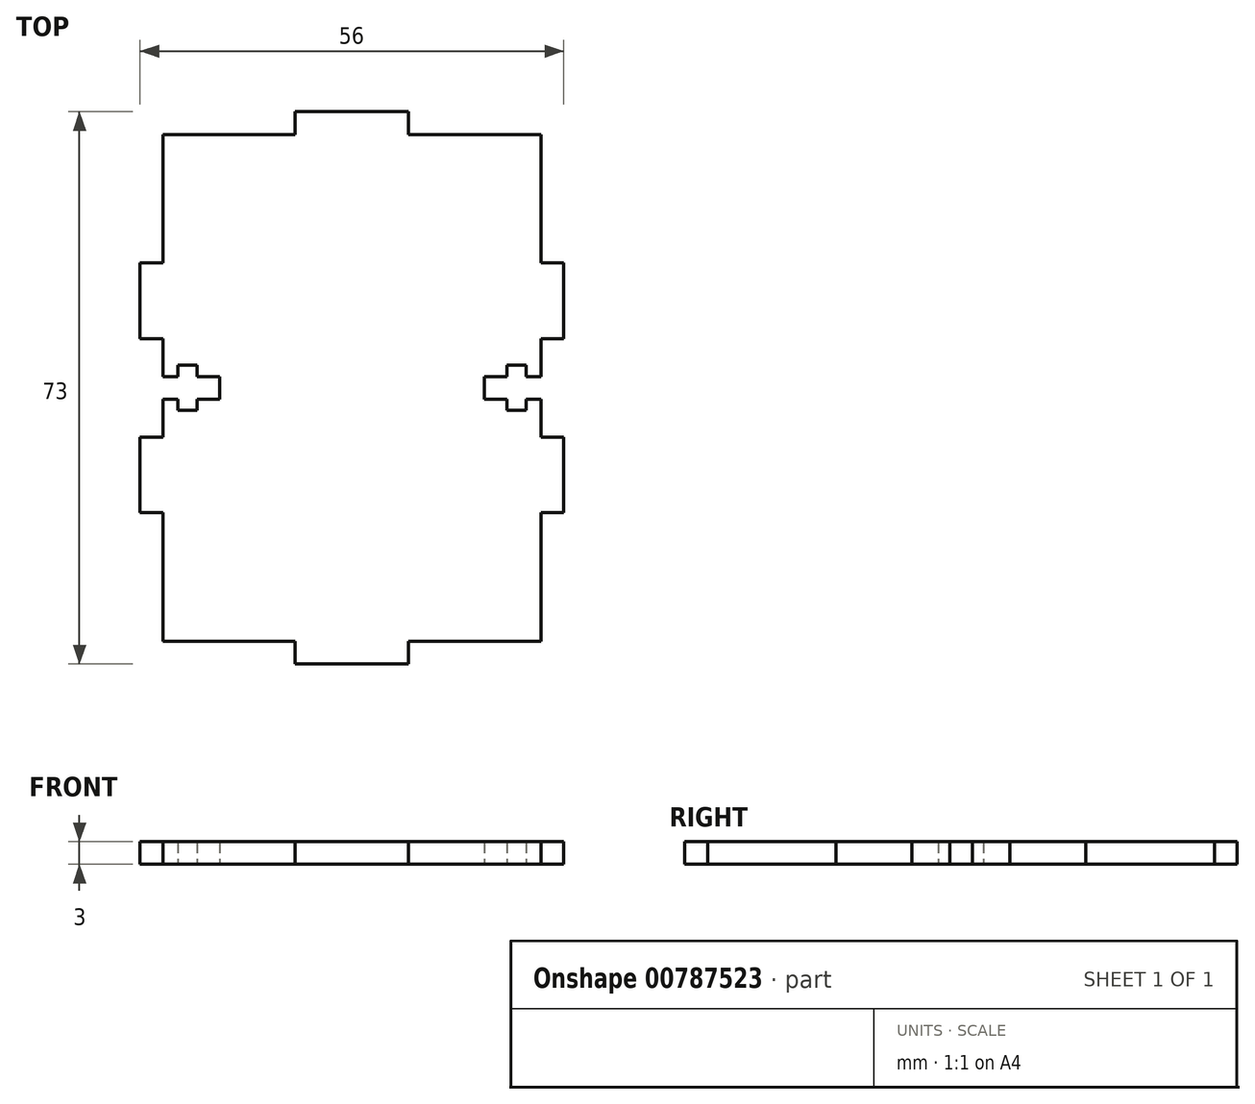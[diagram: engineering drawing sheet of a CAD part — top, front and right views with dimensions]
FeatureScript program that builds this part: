
annotation { "Feature Type Name" : "Feature", "Feature Type Description" : "" }
export const myFeature = defineFeature(function(context is Context, id is Id, definition is map)
    precondition{}
    {
        {
            var Q0;
            Q0=qCreatedBy(makeId("Top.planeOp"),FACE);
            var sketch = newSketch(context, id + "F0", { "sketchPlane" : qUnion([Q0])});
            skLineSegment(sketch, "E0.bottom", {"start": v(-93.46, -6.62) * mm, "end": v(-75.96, -6.62) * mm});
            skLineSegment(sketch, "E0.top", {"start": v(-93.46, -73.62) * mm, "end": v(-75.96, -73.62) * mm});
            skLineSegment(sketch, "E1.bottom", {"start": v(-75.96, -3.62) * mm, "end": v(-60.96, -3.62) * mm});
            skLineSegment(sketch, "E1.left", {"start": v(-75.96, -3.62) * mm, "end": v(-75.96, -6.62) * mm});
            skLineSegment(sketch, "E1.right", {"start": v(-60.96, -3.62) * mm, "end": v(-60.96, -6.62) * mm});
            skPoint(sketch, "E1.middle", {"position": v(-68.46, -6.62) * mm});
            skLineSegment(sketch, "E2.top", {"start": v(-75.96, -76.62) * mm, "end": v(-60.96, -76.62) * mm});
            skLineSegment(sketch, "E2.left", {"start": v(-75.96, -73.62) * mm, "end": v(-75.96, -76.62) * mm});
            skLineSegment(sketch, "E2.right", {"start": v(-60.96, -73.62) * mm, "end": v(-60.96, -76.62) * mm});
            skPoint(sketch, "E2.middle", {"position": v(-68.46, -73.62) * mm});
            skLineSegment(sketch, "E3.trimOffspring", {"start": v(-60.96, -73.62) * mm, "end": v(-43.46, -73.62) * mm});
            skLineSegment(sketch, "E4.trimOffspring", {"start": v(-60.96, -6.62) * mm, "end": v(-43.46, -6.62) * mm});
            skLineSegment(sketch, "E5.trimOffspring", {"start": v(-93.46, -6.62) * mm, "end": v(-93.46, -23.62) * mm});
            skLineSegment(sketch, "E6.trimOffspring", {"start": v(-43.46, -6.62) * mm, "end": v(-43.46, -23.62) * mm});
            skLineSegment(sketch, "E7.0", {"start": v(-93.46, -40.12) * mm, "end": v(-78.46, -40.12) * mm, "construction": true});
            skLineSegment(sketch, "E8", {"start": v(-93.46, -38.62) * mm, "end": v(-91.46, -38.62) * mm});
            skLineSegment(sketch, "E9", {"start": v(-91.46, -38.62) * mm, "end": v(-91.46, -37.12) * mm});
            skLineSegment(sketch, "E10", {"start": v(-91.46, -37.12) * mm, "end": v(-88.96, -37.12) * mm});
            skLineSegment(sketch, "E11", {"start": v(-88.96, -37.12) * mm, "end": v(-88.96, -38.62) * mm});
            skLineSegment(sketch, "E12", {"start": v(-88.96, -38.62) * mm, "end": v(-85.96, -38.62) * mm});
            skLineSegment(sketch, "E13", {"start": v(-85.96, -38.62) * mm, "end": v(-85.96, -41.62) * mm});
            skLineSegment(sketch, "E14", {"start": v(-85.96, -41.62) * mm, "end": v(-88.96, -41.62) * mm});
            skLineSegment(sketch, "E15", {"start": v(-88.96, -41.62) * mm, "end": v(-88.96, -43.12) * mm});
            skLineSegment(sketch, "E16", {"start": v(-88.96, -43.12) * mm, "end": v(-91.46, -43.12) * mm});
            skLineSegment(sketch, "E17", {"start": v(-91.46, -43.12) * mm, "end": v(-91.46, -41.62) * mm});
            skLineSegment(sketch, "E18", {"start": v(-91.46, -41.62) * mm, "end": v(-93.46, -41.62) * mm});
            skLineSegment(sketch, "E19", {"start": v(-93.46, -33.62) * mm, "end": v(-96.46, -33.62) * mm});
            skLineSegment(sketch, "E20", {"start": v(-96.46, -33.62) * mm, "end": v(-96.46, -23.62) * mm});
            skLineSegment(sketch, "E21", {"start": v(-96.46, -23.62) * mm, "end": v(-93.46, -23.62) * mm});
            skLineSegment(sketch, "E22", {"start": v(-93.46, -46.62) * mm, "end": v(-96.46, -46.62) * mm});
            skLineSegment(sketch, "E23", {"start": v(-96.46, -46.62) * mm, "end": v(-96.46, -56.62) * mm});
            skLineSegment(sketch, "E24", {"start": v(-96.46, -56.62) * mm, "end": v(-93.46, -56.62) * mm});
            skLineSegment(sketch, "E25", {"start": v(-43.46, -41.62) * mm, "end": v(-45.46, -41.62) * mm});
            skLineSegment(sketch, "E26", {"start": v(-45.46, -41.62) * mm, "end": v(-45.46, -43.12) * mm});
            skLineSegment(sketch, "E27", {"start": v(-45.46, -43.12) * mm, "end": v(-47.96, -43.12) * mm});
            skLineSegment(sketch, "E28", {"start": v(-47.96, -43.12) * mm, "end": v(-47.96, -41.62) * mm});
            skLineSegment(sketch, "E29", {"start": v(-47.96, -41.62) * mm, "end": v(-50.96, -41.62) * mm});
            skLineSegment(sketch, "E30", {"start": v(-50.96, -41.62) * mm, "end": v(-50.96, -38.62) * mm});
            skLineSegment(sketch, "E31", {"start": v(-50.96, -38.62) * mm, "end": v(-47.96, -38.62) * mm});
            skLineSegment(sketch, "E32", {"start": v(-47.96, -38.62) * mm, "end": v(-47.96, -37.12) * mm});
            skLineSegment(sketch, "E33", {"start": v(-47.96, -37.12) * mm, "end": v(-45.46, -37.12) * mm});
            skLineSegment(sketch, "E34", {"start": v(-45.46, -37.12) * mm, "end": v(-45.46, -38.62) * mm});
            skLineSegment(sketch, "E35", {"start": v(-45.46, -38.62) * mm, "end": v(-43.46, -38.62) * mm});
            skLineSegment(sketch, "E36", {"start": v(-43.46, -46.62) * mm, "end": v(-40.46, -46.62) * mm});
            skLineSegment(sketch, "E37", {"start": v(-40.46, -46.62) * mm, "end": v(-40.46, -56.62) * mm});
            skLineSegment(sketch, "E38", {"start": v(-40.46, -56.62) * mm, "end": v(-43.46, -56.62) * mm});
            skLineSegment(sketch, "E39", {"start": v(-43.46, -33.62) * mm, "end": v(-40.46, -33.62) * mm});
            skLineSegment(sketch, "E40", {"start": v(-40.46, -33.62) * mm, "end": v(-40.46, -23.62) * mm});
            skLineSegment(sketch, "E41", {"start": v(-40.46, -23.62) * mm, "end": v(-43.46, -23.62) * mm});
            skLineSegment(sketch, "E42.trimOffspring", {"start": v(-43.46, -33.62) * mm, "end": v(-43.46, -38.62) * mm});
            skLineSegment(sketch, "E43.trimOffspring", {"start": v(-43.46, -56.62) * mm, "end": v(-43.46, -73.62) * mm});
            skLineSegment(sketch, "E44.trimOffspring", {"start": v(-93.46, -33.62) * mm, "end": v(-93.46, -38.62) * mm});
            skLineSegment(sketch, "E45.trimOffspring", {"start": v(-93.46, -56.62) * mm, "end": v(-93.46, -73.62) * mm});
            skLineSegment(sketch, "E46.trimOffspring", {"start": v(-93.46, -41.62) * mm, "end": v(-93.46, -46.62) * mm});
            skLineSegment(sketch, "E47.trimOffspring", {"start": v(-43.46, -41.62) * mm, "end": v(-43.46, -46.62) * mm});
            skSolve(sketch);
        }
        {
            var Q0;
            Q0=makeQuery(id+"F0.imprint","IMPRINT",FACE,{"disambiguationData":[TD([[makeQuery(id+"F0.imprint","IMPRINT",EDGE,{"derivedFrom":sQuery(id+"F0.wireOp",EDGE,"E0.bottom")}),-1.0]])]});
            extrude(context, id + "F1", {"entities" : qUnion([Q0]), "depth" : 3 * mm, "offsetDistance" : 25.4 * mm});
        }
    });
